# Revit family: ITK 19 Щеточный ввод кабельный ввод 390х115
name_source: partatom
category: Обобщенные модели
revit_build: Autodesk Revit 2016 (Build: 20160314_0715(x64)
units: mm (PartAtom-declared; Revit-internal decimal feet)

## family parameters
Всегда вертикально = Да
Может служить основой для арматурных стержней = Нет
На основе рабочей плоскости = Нет
Общий = Нет
При загрузке вырезать с полостями = Нет
Размер круглого соединителя = Использовать диаметр
Тип детали = Нормальный
Точка расчета площади = Нет

## types (2) — shared parameters
ADSK_Группирование = I. ЩИТЫ И ПУЛЬТЫ
ADSK_Единица измерения = шт
ADSK_Завод-изготовитель = IEK
URL = http://www.itk-group.ru
Высота = 115 мм
Глубина = 11 мм
Изготовитель = ITK
Описание = Горизонтальные щеточные вводы используются для предотвращения попадания пыли внутрь шкафа и на оборудование при его обслуживании, при этом сохраняя возможность вывода коммутационных шнуров и кабелей и подведения их к оборудованию, установленному на 19-дюмовых монтажных профилях. В этом случае кабели выводятся через щеточный ввод.

Щеточные вводы устанавливаются на 19-дюймовые монтажные профили, занимая при этом один или два юнита полезной высоты. Монтаж осуществляется с помощью крепежа винт-шайба-гайка, входящего в комплект поставки.
Совместимы со всеми 19-дюймовыми шкафами и стойками ITK.
Обладают современным привлекательным дизайном и продуманной конструкцией.
Удобны в монтаже и эксплуатации.
Соответствие международным стандартам ISO9001, IEC 297, ISO/IEC 11801. 
Сертифицированы по ГОСТ Р.
Все аксессуары идут с крепежом.
Возможно исполнение в двух цветах: серый (RAL7035) и черный (RAL9005).
Всегда в наличии на складе.
Гарантия на все аксессуары до 2-х лет.
Ширина = 390 мм
zero-valued in all types: ADSK_Масса

## per-type parameters (varying)
| type | ADSK_Наименование | Материал |
| BE05-390-115M | ITK Щеточный кабельный ввод 390х115 мм, черный | Окраска - RAL 9005 |
| BE35-390-115M | ITK Щеточный кабельный ввод 390х115 мм, серый | Окраска - RAL 7035 |

note: column(s) folded — value = type name in every type: ADSK_Марка, ADSK_Наименование краткое
